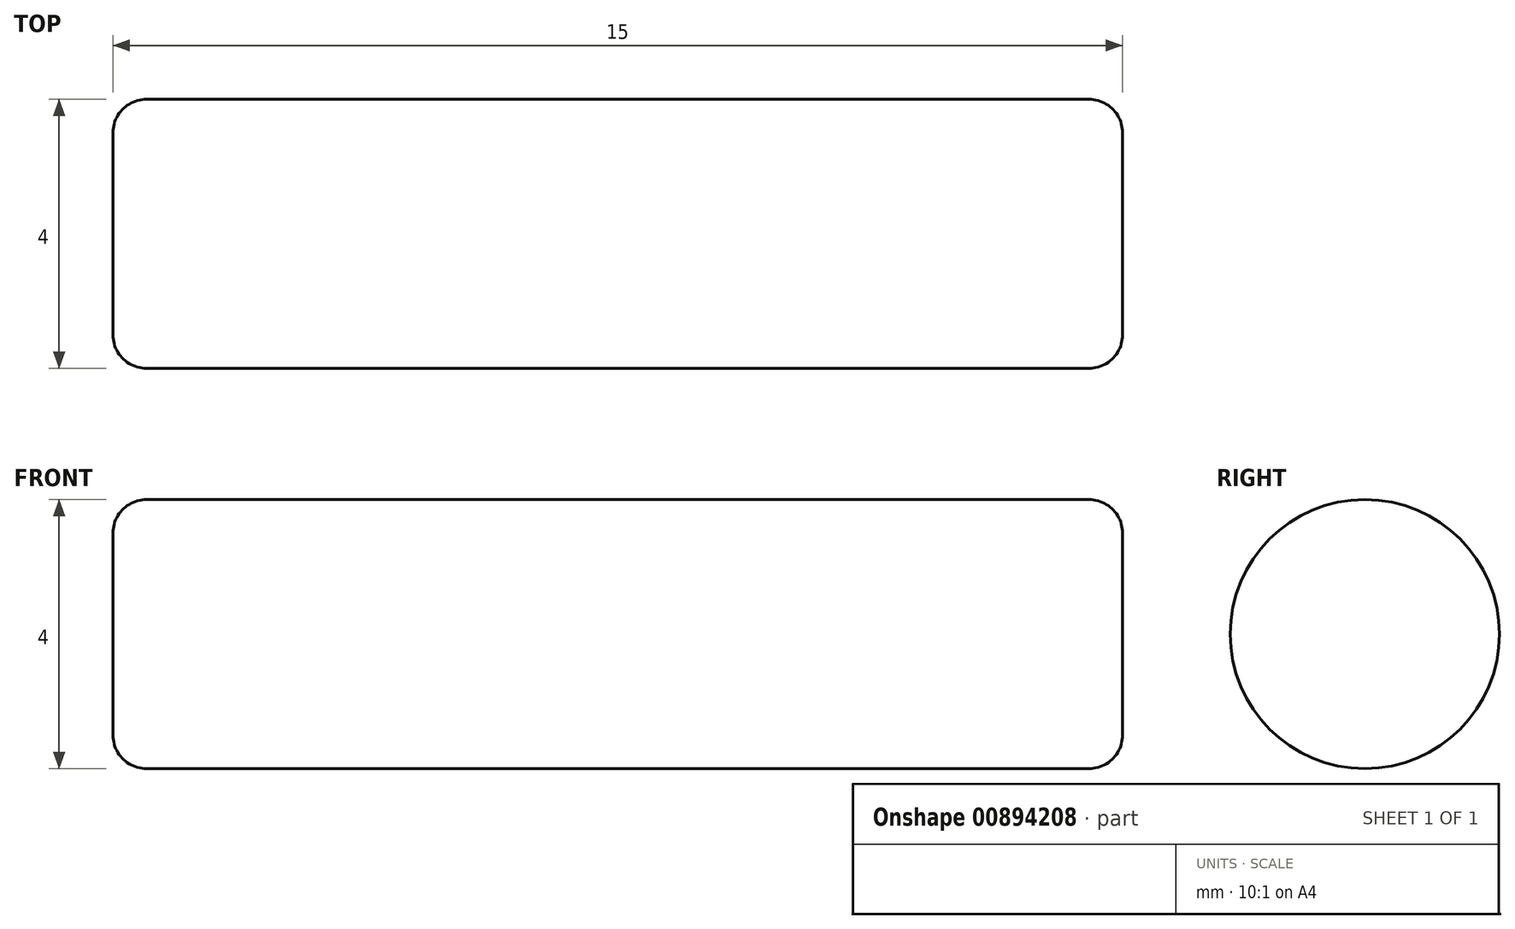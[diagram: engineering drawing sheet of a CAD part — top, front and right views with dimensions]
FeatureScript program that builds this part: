
annotation { "Feature Type Name" : "Feature", "Feature Type Description" : "" }
export const myFeature = defineFeature(function(context is Context, id is Id, definition is map)
    precondition{}
    {
        {
            var Q0;
            Q0=qCreatedBy(makeId("Front.planeOp"),FACE);
            var sketch = newSketch(context, id + "F0", { "sketchPlane" : qUnion([Q0])});
            skLineSegment(sketch, "E0", {"start": v(0, 0) * mm, "end": v(0, 1.5) * mm});
            skLineSegment(sketch, "E1", {"start": v(0.5, 2) * mm, "end": v(14.5, 2) * mm});
            skLineSegment(sketch, "E2", {"start": v(15, 1.5) * mm, "end": v(15, 0) * mm});
            skLineSegment(sketch, "E3", {"start": v(15, 0) * mm, "end": v(0, 0) * mm});
            skPoint(sketch, "E4.visualSharp", {"position": v(15, 2) * mm});
            skArc(sketch, "E4.filletArc", {"start": v(15, 1.5) * mm, "mid": v(14.85, 1.85) * mm, "end": v(14.5, 2) * mm});
            skPoint(sketch, "E5.visualSharp", {"position": v(0, 2) * mm});
            skArc(sketch, "E5.filletArc", {"start": v(0.5, 2) * mm, "mid": v(0.15, 1.85) * mm, "end": v(0, 1.5) * mm});
            skSolve(sketch);
        }
        {
            var Q0;
            Q0=makeQuery(id+"F0.imprint","IMPRINT",FACE,{"disambiguationData":[TD([[makeQuery(id+"F0.imprint","IMPRINT",EDGE,{"derivedFrom":sQuery(id+"F0.wireOp",EDGE,"E0")}),-1.0]])]});
            var Q1;
            Q1=sQuery(id+"F0.wireOp",EDGE,"E3");
            revolve(context, id + "F1", {"surfaceOperationType" : NewSurfaceOperationType.NEW, "entities" : qUnion([Q0]), "axis" : qUnion([Q1]), "revolveType" : RevolveType.FULL});
        }
    });
